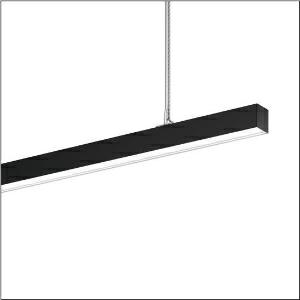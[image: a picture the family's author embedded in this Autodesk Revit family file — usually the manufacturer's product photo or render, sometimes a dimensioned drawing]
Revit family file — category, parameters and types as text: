
# Revit family: silica_r__21_51mx33tat7b_231b
name_source: partatom
category: Lighting Fixtures
units: mm (PartAtom-declared; Revit-internal decimal feet)

## family parameters
Cut with Voids When Loaded = No
Host = Face
Light Source = No
Part Type = Normal
Room Calculation Point = No
Round Connector Dimension = Use Diameter
Shared = No

## types (1)
- --- (1 x LED, 5740 lm, 53.8 W, 6500K)
    Apparent Load = 54 VA
    CIE Flux Codes = 78 96 99 56 100
    Color Rendering = 80
    Color Temperature = 6500K
    Default Elevation = 1800 mm
    Description = Silica® 21, office luminaire, primary optical cover: prismatic diffuser, of PMMA, CAT 2 (L<= 3000cd/m²), light emission: direct/indirect distribution, primary light characteristic: symmetric, installation type: suspended mounting, LED, rated luminous flux: 5.740lm, luminous efficacy: 102lm/W, light colour: 8tw, colour temperature: 2700..6500K, control gear: ECG DALI, with terminal, 3+2-pole, max. 2.5mm², mains connection: 220..240V, AC, 50/60Hz, rated input power: 56.5W, luminaire housing, of aluminium, jet black (RAL 9005), length: 1.204mm, width: 53mm, height: 53mm, protection rating (complete): IP20, insulation class (complete): insulation class I (protective earthing), certification: CE, permissible operating ambient temperature: 0..+35°C, standard: EN 50419, packaging unit: 1 piece
    Height = 53 mm
    Lamp = 1 x LED
    Lamp Light Flux = 5740 lm
    Lamp Power = 53.8 W
    Lamp count = 1
    Length = 1204 mm
    Luminous efficacy = 107 lm/W
    Manufacturer = Siteco
    ModVariant = No
    Model = 51MX33TAT7B
    Mounting Place = Ceiling
    Mounting Type = Pendant
    Number of Poles = 1
    OnlyDefault = Yes
    Power Factor = 1
    Product Name = Silica® 21
    Product group = office luminaire | ceiling pendant
    ProductGroupID = 902
    Protection Class = Protection class I
    Protection Degree = IP 20
    RLX_Detail_Level = 1
    RLX_Emergency_Light_Flux = 0 lm
    RLX_Emergency_Type = 0
    RLX_Emergency_Type_DB = No
    RlxData = <blob elided: 22905 chars, md5=e27dc022>
    Socket = socket
    Standby Power = 0 W
    System Light Flux = 5740 lm
    System Power = 54 W
    Type Comments = individual setting
    Type Image = l_1335856.jpg
    URL = http://relux.com
    VarID = @adj_109567
    Voltage = 0 V
    Weight = 0.00 kg
    Width = 53 mm

## geometry (parser evidence)
native form markers: Blend x4, Sweep x13
no freeform markers — native parametric forms only
